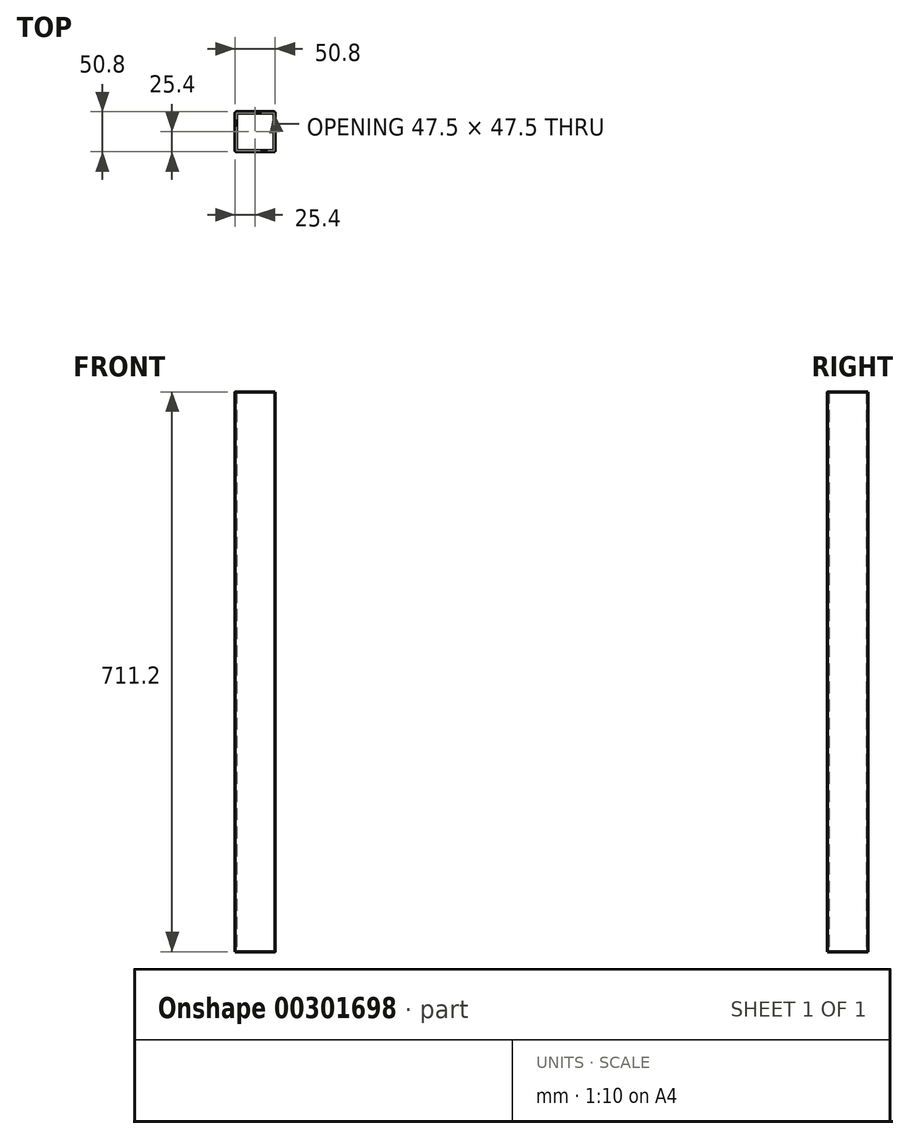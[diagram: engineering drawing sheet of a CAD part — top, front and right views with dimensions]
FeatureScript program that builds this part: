
annotation { "Feature Type Name" : "Feature", "Feature Type Description" : "" }
export const myFeature = defineFeature(function(context is Context, id is Id, definition is map)
    precondition{}
    {
        {
            var Q0;
            Q0=qCreatedBy(makeId("Top.planeOp"),FACE);
            var sketch = newSketch(context, id + "F0", { "sketchPlane" : qUnion([Q0])});
            skLineSegment(sketch, "E0.bottom", {"start": v(-23.75, -25.4) * mm, "end": v(23.75, -25.4) * mm});
            skLineSegment(sketch, "E0.top", {"start": v(-23.75, 25.4) * mm, "end": v(23.75, 25.4) * mm});
            skLineSegment(sketch, "E0.left", {"start": v(-25.4, -23.75) * mm, "end": v(-25.4, 23.75) * mm});
            skLineSegment(sketch, "E0.right", {"start": v(25.4, -23.75) * mm, "end": v(25.4, 23.75) * mm});
            skPoint(sketch, "E0.middle", {"position": v(0, 0) * mm});
            skLineSegment(sketch, "E1.0", {"start": v(-22.1, 23.75) * mm, "end": v(22.1, 23.75) * mm});
            skLineSegment(sketch, "E1.1", {"start": v(-23.75, -22.1) * mm, "end": v(-23.75, 22.1) * mm});
            skLineSegment(sketch, "E1.2", {"start": v(-22.1, -23.75) * mm, "end": v(22.1, -23.75) * mm});
            skLineSegment(sketch, "E1.3", {"start": v(23.75, -22.1) * mm, "end": v(23.75, 22.1) * mm});
            skPoint(sketch, "E2.visualSharp", {"position": v(-23.75, 23.75) * mm});
            skArc(sketch, "E2.filletArc", {"start": v(-22.1, 23.75) * mm, "mid": v(-23.27, 23.27) * mm, "end": v(-23.75, 22.1) * mm});
            skPoint(sketch, "E3.visualSharp", {"position": v(23.75, 23.75) * mm});
            skArc(sketch, "E3.filletArc", {"start": v(23.75, 22.1) * mm, "mid": v(23.27, 23.27) * mm, "end": v(22.1, 23.75) * mm});
            skPoint(sketch, "E4.visualSharp", {"position": v(23.75, -23.75) * mm});
            skArc(sketch, "E4.filletArc", {"start": v(22.1, -23.75) * mm, "mid": v(23.27, -23.27) * mm, "end": v(23.75, -22.1) * mm});
            skPoint(sketch, "E5.visualSharp", {"position": v(-23.75, -23.75) * mm});
            skArc(sketch, "E5.filletArc", {"start": v(-23.75, -22.1) * mm, "mid": v(-23.27, -23.27) * mm, "end": v(-22.1, -23.75) * mm});
            skPoint(sketch, "E6.visualSharp", {"position": v(-25.4, -25.4) * mm});
            skArc(sketch, "E6.filletArc", {"start": v(-25.4, -23.75) * mm, "mid": v(-24.92, -24.92) * mm, "end": v(-23.75, -25.4) * mm});
            skPoint(sketch, "E7.visualSharp", {"position": v(-25.4, 25.4) * mm});
            skArc(sketch, "E7.filletArc", {"start": v(-23.75, 25.4) * mm, "mid": v(-24.92, 24.92) * mm, "end": v(-25.4, 23.75) * mm});
            skPoint(sketch, "E8.visualSharp", {"position": v(25.4, 25.4) * mm});
            skArc(sketch, "E8.filletArc", {"start": v(25.4, 23.75) * mm, "mid": v(24.92, 24.92) * mm, "end": v(23.75, 25.4) * mm});
            skPoint(sketch, "E9.visualSharp", {"position": v(25.4, -25.4) * mm});
            skArc(sketch, "E9.filletArc", {"start": v(23.75, -25.4) * mm, "mid": v(24.92, -24.92) * mm, "end": v(25.4, -23.75) * mm});
            skSolve(sketch);
        }
        {
            var Q0;
            Q0=makeQuery(id+"F0.imprint","IMPRINT",FACE,{"disambiguationData":[TD([[makeQuery(id+"F0.imprint","IMPRINT",EDGE,{"derivedFrom":sQuery(id+"F0.wireOp",EDGE,"E0.bottom")}),1.0]])]});
            extrude(context, id + "F1", {"entities" : qUnion([Q0]), "depth" : 711.2 * mm});
        }
    });
